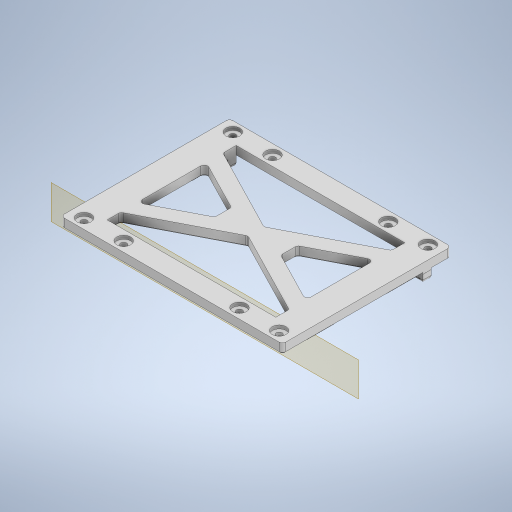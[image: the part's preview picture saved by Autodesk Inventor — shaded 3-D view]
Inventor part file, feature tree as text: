
AUTODESK INVENTOR PART (.ipt)
format: ipt  version: 2024.3 (Build 283343000, 343)  size: 672,768 bytes
history: native  units: in
note: dims shown in document units (in); Inventor stores cm internally (conversion verified against a paired STEP export)
features: sketch x10, extrude x8, fillet x6, reference x6, chamfer x4, other x3, hole x2, projected_geometry x2, plane x1
ambient origin geometry x8: Origin, YZ Plane, XZ Plane, XY Plane, X Axis, Y Axis, Z Axis, Center Point
bodies: Solid1 (feature_tree)
feature tree (42):
  plane  "Work Plane1"
  extrude  "Extrusion1"  Depth=0.0118in
  extrude  "Extrusion2"  Depth=0.315in
  extrude  "Extrusion3"  Depth=0.0079in
  extrude  "Extrusion4"  Depth=2.5197in TaperAngle=0.0deg
  chamfer  "Chamfer3"  Distance=0.0787in
  extrude  "Extrusion5"  Depth=0.7087in TaperAngle=0.0deg
  extrude  "Extrusion8"  Depth=0.7874in
  hole  "Hole3"  [1 undecoded]
  hole  "Hole4"  [1 undecoded]
  fillet  "Fillet2"  Radius=0.7087in
  extrude  "Extrusion6"  Depth=0.2362in
  fillet  "Fillet3"  Radius=0.0787in
  fillet  "Fillet4"  Radius=0.1969in
  fillet  "Fillet5"  Radius=0.1969in
  chamfer  "Chamfer4"  Distance=0.0787in
  fillet  "Fillet6"  Radius=0.0787in
  extrude  "Extrusion7"  Depth=0.3937in
  chamfer  "Chamfer5"  Distance=0.0394in Angle=45.0deg
  fillet  "Fillet7"  Radius=0.0394in
  chamfer  "Chamfer6"  Distance=0.7874in
  sketch  "Sketch1"  dims[d1=0.0197in d2=0.0118in]
  reference  "Reference1"
  reference  "Reference2"
  reference  "Reference3"
  reference  "Reference4"
  reference  "Reference5"
  sketch  "Sketch2"  dims[d3=0.2362in d4=0.315in]
  sketch  "Sketch4"  dims[d5=0.0079in d6=0.0079in]
  projected_geometry  "Projected Loop1"
  reference  "Reference6"
  projected_geometry  "Projected Loop2"
  sketch  "Sketch6"  dims[d7=0.0079in d8=2.5197in d9=0.0in d11=0.0787in d12=0.0in]
  sketch  "Sketch7"  dims[d22=0.7087in d23=0.0in d38=0.7087in d39=0.0in]
  sketch  "Sketch8"  dims[d40=0.0787in d41=0.0787in d42=45.0deg d43=0.7874in]
  sketch  "Sketch9"  dims[d44=0.7874in d45=0.3937in]
  sketch  "Sketch10"  dims[d46=0.0394in d48=0.3937in d49=0.7087in d50=0.0in]
  sketch  "Sketch11"  dims[d51=0.2362in d52=0.2362in]
  sketch  "Sketch13"  dims[d53=0.1417in d54=0.2362in d55=0.3307in d56=0.0787in d57=90.0deg d58=0.315in d59=0.8108in d60=0.1417in d61=0.2362in d62=0.3307in d63=0.0787in d64=90.0deg d65=0.315in d66=0.8108in d67=0.0787in d68=0.1969in d69=0.1969in d70=0.0in d71=0.0787in d72=0.0787in d73=0.0787in d74=0.0394in d75=0.0787in d76=45.0deg d78=0.0394in d80=0.7874in d81=0.7874in d82=0.3937in d83=0.0in d84=0.0787in d85=0.0787in d86=45.0deg d87=0.0787in d88=0.4724in d89=0.4724in d90=0.1969in d91=0.0in d92=1.378in d93=1.378in d94=0.0394in d95=0.0787in d96=0.0787in d97=45.0deg]
  other  "<userpath>\Dropbox\elec\Mechanical\DCBuddyV2\PCB\_TOP_Design.iam"
  other  "_TOP_Design.iam"
  other  "DCB2_BottomShell:1"
note: 2 required parameter values undecoded (feature->parameter linkage not recoverable at this tier; creation-order binding heuristic only, values carry confidence <= 0.55)
